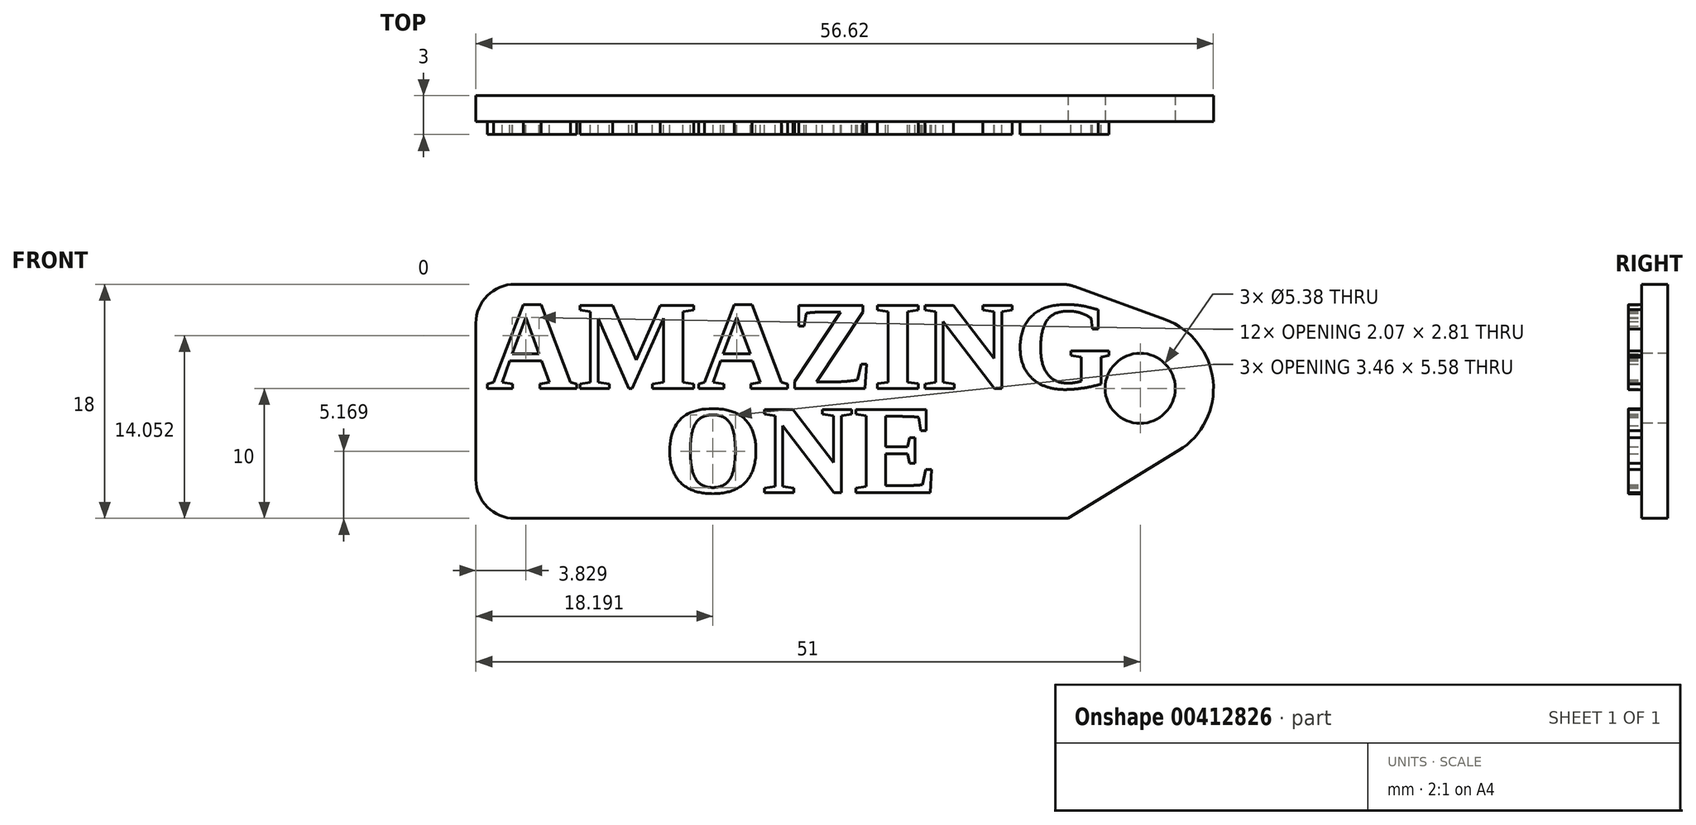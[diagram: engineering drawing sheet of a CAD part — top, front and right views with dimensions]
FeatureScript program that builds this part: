
annotation { "Feature Type Name" : "Feature", "Feature Type Description" : "" }
export const myFeature = defineFeature(function(context is Context, id is Id, definition is map)
    precondition{}
    {
        {
            var Q0;
            Q0=qCreatedBy(makeId("Front.planeOp"),FACE);
            var sketch = newSketch(context, id + "F0", { "sketchPlane" : qUnion([Q0])});
            skText(sketch, "E0", { "text": "AMAZING\n", "fontName": "Tinos-Bold.ttf"});
            const initialGuessF0  = {"E0": [-0.0242, -0.007, 1, 0, 0.007]};
            skSetInitialGuess(sketch, initialGuessF0);
            skSolve(sketch);
        }
        {
            var Q0;
            Q0=qSketchRegion(id+"F0",true);
            extrude(context, id + "F1", {"entities" : qUnion([Q0]), "depth" : 1 * mm});
        }
        {
            var Q0;
            Q0=qCreatedBy(makeId("Front.planeOp"),FACE);
            var sketch = newSketch(context, id + "F2", { "sketchPlane" : qUnion([Q0])});
            skText(sketch, "E1", { "text": "ONE", "fontName": "Tinos-Bold.ttf"});
            const initialGuessF2  = {"E1": [-0.01059, -0.015, 1, 0, 0.007]};
            skSetInitialGuess(sketch, initialGuessF2);
            skSolve(sketch);
        }
        {
            var Q0;
            Q0 = qSketchRegion(id + "F2", true);
            var Q1;
            Q1=makeQuery(id+"F1.opExtrude","CAP_FACE",FACE,{"disambiguationData":[OSD([sQuery(id+"F0.wireOp",EDGE,"E0.sketch_text.stroke-0"),sQuery(id+"F0.wireOp",EDGE,"E0.sketch_text.stroke-1"),sQuery(id+"F0.wireOp",EDGE,"E0.sketch_text.stroke-2"),sQuery(id+"F0.wireOp",EDGE,"E0.sketch_text.stroke-3"),sQuery(id+"F0.wireOp",EDGE,"E0.sketch_text.stroke-4"),sQuery(id+"F0.wireOp",EDGE,"E0.sketch_text.stroke-5"),sQuery(id+"F0.wireOp",EDGE,"E0.sketch_text.stroke-6"),sQuery(id+"F0.wireOp",EDGE,"E0.sketch_text.stroke-7"),sQuery(id+"F0.wireOp",EDGE,"E0.sketch_text.stroke-8"),sQuery(id+"F0.wireOp",EDGE,"E0.sketch_text.stroke-9"),sQuery(id+"F0.wireOp",EDGE,"E0.sketch_text.stroke-10"),sQuery(id+"F0.wireOp",EDGE,"E0.sketch_text.stroke-11"),sQuery(id+"F0.wireOp",EDGE,"E0.sketch_text.stroke-12"),sQuery(id+"F0.wireOp",EDGE,"E0.sketch_text.stroke-13"),sQuery(id+"F0.wireOp",EDGE,"E0.sketch_text.stroke-14"),sQuery(id+"F0.wireOp",EDGE,"E0.sketch_text.stroke-15"),sQuery(id+"F0.wireOp",EDGE,"E0.sketch_text.stroke-16"),sQuery(id+"F0.wireOp",EDGE,"E0.sketch_text.stroke-17"),sQuery(id+"F0.wireOp",EDGE,"E0.sketch_text.stroke-18"),sQuery(id+"F0.wireOp",EDGE,"E0.sketch_text.stroke-19"),sQuery(id+"F0.wireOp",EDGE,"E0.sketch_text.stroke-20"),sQuery(id+"F0.wireOp",EDGE,"E0.sketch_text.stroke-21"),sQuery(id+"F0.wireOp",EDGE,"E0.sketch_text.stroke-22"),sQuery(id+"F0.wireOp",EDGE,"E0.sketch_text.stroke-23"),sQuery(id+"F0.wireOp",EDGE,"E0.sketch_text.stroke-24"),sQuery(id+"F0.wireOp",EDGE,"E0.sketch_text.stroke-25"),sQuery(id+"F0.wireOp",EDGE,"E0.sketch_text.stroke-26"),sQuery(id+"F0.wireOp",EDGE,"E0.sketch_text.stroke-27"),sQuery(id+"F0.wireOp",EDGE,"E0.sketch_text.stroke-28"),sQuery(id+"F0.wireOp",EDGE,"E0.sketch_text.stroke-29"),sQuery(id+"F0.wireOp",EDGE,"E0.sketch_text.stroke-30"),sQuery(id+"F0.wireOp",EDGE,"E0.sketch_text.stroke-31"),sQuery(id+"F0.wireOp",EDGE,"E0.sketch_text.stroke-32"),sQuery(id+"F0.wireOp",EDGE,"E0.sketch_text.stroke-33"),sQuery(id+"F0.wireOp",EDGE,"E0.sketch_text.stroke-34"),sQuery(id+"F0.wireOp",EDGE,"E0.sketch_text.stroke-35"),sQuery(id+"F0.wireOp",EDGE,"E0.sketch_text.stroke-36"),sQuery(id+"F0.wireOp",EDGE,"E0.sketch_text.stroke-37"),sQuery(id+"F0.wireOp",EDGE,"E0.sketch_text.stroke-38")])],"isStart":false});
            extrude(context, id + "F3", {"entities" : qUnion([Q0]), "endBound" : BoundingType.UP_TO_SURFACE, "endBoundEntityFace" : qUnion([Q1]), "depth" : 25 * mm});
        }
        {
            var Q0;
            Q0=qCreatedBy(makeId("Front.planeOp"),FACE);
            var sketch = newSketch(context, id + "F4", { "sketchPlane" : qUnion([Q0])});
            skLineSegment(sketch, "E2", {"start": v(-25, 1) * mm, "end": v(20.47, 1) * mm});
            skLineSegment(sketch, "E3", {"start": v(-25, -17) * mm, "end": v(-25, 1) * mm});
            skCircle(sketch, "E4", {"center": v(26, -7) * mm, "radius": 5.62 * mm});
            skPoint(sketch, "E5.endSnap0", {"position": v(21.2, -7) * mm});
            skCircle(sketch, "E6", {"center": v(26, -7) * mm, "radius": 2.69 * mm});
            skLineSegment(sketch, "E7.0", {"start": v(-24.2, -7) * mm, "end": v(-24.2, 0) * mm, "construction": true});
            skLineSegment(sketch, "E8", {"start": v(-24.26, -3.5) * mm, "end": v(-24.2, -3.5) * mm, "construction": true});
            skLineSegment(sketch, "E9", {"start": v(20.47, 1) * mm, "end": v(27.92, -1.71) * mm});
            skLineSegment(sketch, "E10", {"start": v(-25, -17) * mm, "end": v(20.47, -17) * mm});
            skLineSegment(sketch, "E11", {"start": v(20.47, -17) * mm, "end": v(28.94, -11.8) * mm});
            skSolve(sketch);
        }
        {
            var Q0;
            Q0=qSketchRegion(id+"F4",true);
            extrude(context, id + "F5", {"entities" : qUnion([Q0]), "oppositeDirection" : true, "depth" : 2 * mm});
        }
        {
            var Q0;
            Q0 = qSketchRegion(id + "F0", true);
            var Q1;
            Q1=makeQuery(id+"F1.opExtrude","CAP_FACE",FACE,{"disambiguationData":[OSD([sQuery(id+"F0.wireOp",EDGE,"E0.sketch_text.stroke-71"),sQuery(id+"F0.wireOp",EDGE,"E0.sketch_text.stroke-72"),sQuery(id+"F0.wireOp",EDGE,"E0.sketch_text.stroke-73"),sQuery(id+"F0.wireOp",EDGE,"E0.sketch_text.stroke-74"),sQuery(id+"F0.wireOp",EDGE,"E0.sketch_text.stroke-75"),sQuery(id+"F0.wireOp",EDGE,"E0.sketch_text.stroke-76"),sQuery(id+"F0.wireOp",EDGE,"E0.sketch_text.stroke-77"),sQuery(id+"F0.wireOp",EDGE,"E0.sketch_text.stroke-78"),sQuery(id+"F0.wireOp",EDGE,"E0.sketch_text.stroke-79"),sQuery(id+"F0.wireOp",EDGE,"E0.sketch_text.stroke-80"),sQuery(id+"F0.wireOp",EDGE,"E0.sketch_text.stroke-81"),sQuery(id+"F0.wireOp",EDGE,"E0.sketch_text.stroke-82"),sQuery(id+"F0.wireOp",EDGE,"E0.sketch_text.stroke-83"),sQuery(id+"F0.wireOp",EDGE,"E0.sketch_text.stroke-84"),sQuery(id+"F0.wireOp",EDGE,"E0.sketch_text.stroke-85"),sQuery(id+"F0.wireOp",EDGE,"E0.sketch_text.stroke-86"),sQuery(id+"F0.wireOp",EDGE,"E0.sketch_text.stroke-87"),sQuery(id+"F0.wireOp",EDGE,"E0.sketch_text.stroke-88"),sQuery(id+"F0.wireOp",EDGE,"E0.sketch_text.stroke-89"),sQuery(id+"F0.wireOp",EDGE,"E0.sketch_text.stroke-90"),sQuery(id+"F0.wireOp",EDGE,"E0.sketch_text.stroke-91"),sQuery(id+"F0.wireOp",EDGE,"E0.sketch_text.stroke-92"),sQuery(id+"F0.wireOp",EDGE,"E0.sketch_text.stroke-93"),sQuery(id+"F0.wireOp",EDGE,"E0.sketch_text.stroke-94"),sQuery(id+"F0.wireOp",EDGE,"E0.sketch_text.stroke-95"),sQuery(id+"F0.wireOp",EDGE,"E0.sketch_text.stroke-96"),sQuery(id+"F0.wireOp",EDGE,"E0.sketch_text.stroke-97"),sQuery(id+"F0.wireOp",EDGE,"E0.sketch_text.stroke-98"),sQuery(id+"F0.wireOp",EDGE,"E0.sketch_text.stroke-99"),sQuery(id+"F0.wireOp",EDGE,"E0.sketch_text.stroke-100"),sQuery(id+"F0.wireOp",EDGE,"E0.sketch_text.stroke-101"),sQuery(id+"F0.wireOp",EDGE,"E0.sketch_text.stroke-102"),sQuery(id+"F0.wireOp",EDGE,"E0.sketch_text.stroke-103"),sQuery(id+"F0.wireOp",EDGE,"E0.sketch_text.stroke-104"),sQuery(id+"F0.wireOp",EDGE,"E0.sketch_text.stroke-105"),sQuery(id+"F0.wireOp",EDGE,"E0.sketch_text.stroke-106"),sQuery(id+"F0.wireOp",EDGE,"E0.sketch_text.stroke-107"),sQuery(id+"F0.wireOp",EDGE,"E0.sketch_text.stroke-108"),sQuery(id+"F0.wireOp",EDGE,"E0.sketch_text.stroke-109")])],"isStart":false});
            extrude(context, id + "F6", {"entities" : qUnion([Q0]), "endBound" : BoundingType.UP_TO_SURFACE, "endBoundEntityFace" : qUnion([Q1]), "depth" : 25 * mm});
        }
        {
            var Q0;
            Q0=makeQuery(id+"F5.opExtrude","SWEPT_EDGE",EDGE,{"disambiguationData":[OSD([sQuery(id+"F4.wireOp",EDGE,"E2"),sQuery(id+"F4.wireOp",EDGE,"E3")])]});
            var Q1;
            Q1=makeQuery(id+"F5.opExtrude","SWEPT_EDGE",EDGE,{"disambiguationData":[OSD([sQuery(id+"F4.wireOp",EDGE,"HxKfLjwR-2V6p-J2cI-nbav-LqhWMXN5vdWp"),sQuery(id+"F4.wireOp",EDGE,"E3")])]});
            var Q2;
            Q2=makeQuery(id+"F5.opExtrude","SWEPT_EDGE",EDGE,{"disambiguationData":[OSD([sQuery(id+"F4.wireOp",EDGE,"HxKfLjwR-2V6p-J2cI-nbav-LqhWMXN5vdWp"),sQuery(id+"F4.wireOp",EDGE,"yqddGZYT-9OCD-ybmd-QjBU-P8vNbqM37v9X")])]});
            var Q3;
            Q3=makeQuery(id+"F5.opExtrude","SWEPT_EDGE",EDGE,{"disambiguationData":[OSD([sQuery(id+"F4.wireOp",EDGE,"E2"),sQuery(id+"F4.wireOp",EDGE,"g5F0nNYr-RwvK-rXGj-4yFg-44NqVEQ25fOh")])]});
            fillet(context, id + "F7", {"entities" : qUnion([Q0, Q1, Q2, Q3]), "radius" : 3 * mm, "tangentPropagation" : true, "allowEdgeOverflow" : false});
        }
        {
            var Q0;
            Q0=makeQuery(id+"F5.opExtrude","CAP_FACE",FACE,{"disambiguationData":[OSD([sQuery(id+"F4.wireOp",EDGE,"HxKfLjwR-2V6p-J2cI-nbav-LqhWMXN5vdWp"),sQuery(id+"F4.wireOp",EDGE,"E2"),sQuery(id+"F4.wireOp",EDGE,"E3"),sQuery(id+"F4.wireOp",EDGE,"E4"),sQuery(id+"F4.wireOp",EDGE,"g5F0nNYr-RwvK-rXGj-4yFg-44NqVEQ25fOh"),sQuery(id+"F4.wireOp",EDGE,"yqddGZYT-9OCD-ybmd-QjBU-P8vNbqM37v9X"),sQuery(id+"F4.wireOp",EDGE,"E6")])],"isStart":true});
            var sketch = newSketch(context, id + "F8", { "sketchPlane" : qUnion([Q0])});
            skCircle(sketch, "E12", {"center": v(26, -7) * mm, "radius": 5.62 * mm});
            skSolve(sketch);
        }
        {
            var Q0;
            {var subQ0=sQuery(id+"F4.wireOp",EDGE,"E11");var subQ6=makeQuery(id+"F5.opExtrude","CAP_EDGE",EDGE,{"disambiguationData":[OSD([subQ0])],"isStart":true});Q0=makeQuery(id+"F8.imprint","IMPRINT",FACE,{"disambiguationData":[TD([[makeQuery(id+"F8.imprint","IMPRINT",EDGE,{"derivedFrom":subQ6}),1.0]])]});}
            cPlane(context, id + "F9", {"entities" : qUnion([Q0]), "cplaneType" : CPlaneType.OFFSET, "offset" : 1.3 * mm, "oppositeDirection" : true, "width" : 150 * mm, "height" : 150 * mm});
        }
    });
